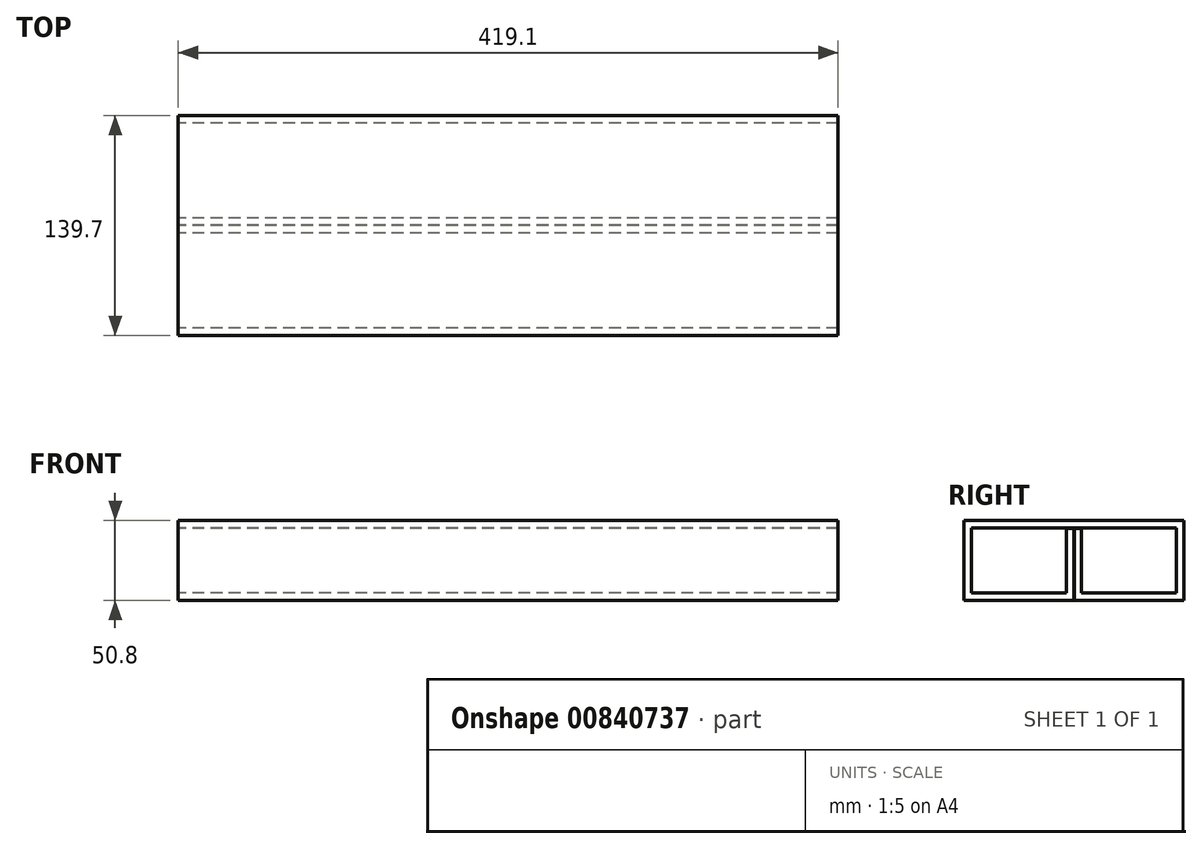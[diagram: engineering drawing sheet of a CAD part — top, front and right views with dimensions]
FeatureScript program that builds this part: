
annotation { "Feature Type Name" : "Feature", "Feature Type Description" : "" }
export const myFeature = defineFeature(function(context is Context, id is Id, definition is map)
    precondition{}
    {
        {
            var Q0;
            Q0=qCreatedBy(makeId("Right.planeOp"),FACE);
            var sketch = newSketch(context, id + "F0", { "sketchPlane" : qUnion([Q0])});
            skLineSegment(sketch, "E0", {"start": v(0, 0) * mm, "end": v(0, 126.35) * mm, "construction": true});
            skLineSegment(sketch, "E1.bottom", {"start": v(-69.85, 50.8) * mm, "end": v(69.85, 50.8) * mm});
            skLineSegment(sketch, "E1.top", {"start": v(-69.85, 0) * mm, "end": v(-0.13, 0) * mm});
            skLineSegment(sketch, "E1.left", {"start": v(-69.85, 50.8) * mm, "end": v(-69.85, 0) * mm});
            skLineSegment(sketch, "E2.0", {"start": v(-65.09, 46.04) * mm, "end": v(65.09, 46.04) * mm});
            skLineSegment(sketch, "E2.1", {"start": v(-65.09, 46.04) * mm, "end": v(-65.09, 4.76) * mm});
            skLineSegment(sketch, "E2.2", {"start": v(-65.09, 4.76) * mm, "end": v(-4.76, 4.76) * mm});
            skLineSegment(sketch, "E2.3", {"start": v(-4.76, 45.78) * mm, "end": v(-4.76, 4.76) * mm});
            skLineSegment(sketch, "E3.MirrorCS", {"start": v(69.85, 50.8) * mm, "end": v(69.85, 0) * mm});
            skLineSegment(sketch, "E4.MirrorCS", {"start": v(4.76, 45.78) * mm, "end": v(4.76, 4.76) * mm});
            skLineSegment(sketch, "E5.MirrorCS", {"start": v(65.09, 4.76) * mm, "end": v(4.76, 4.76) * mm});
            skLineSegment(sketch, "E6.MirrorCS", {"start": v(65.09, 46.04) * mm, "end": v(65.09, 4.76) * mm});
            skLineSegment(sketch, "E7.left", {"start": v(-0.13, 0) * mm, "end": v(-0.13, 45.78) * mm});
            skLineSegment(sketch, "E7.right", {"start": v(0.13, 0) * mm, "end": v(0.13, 45.78) * mm});
            skLineSegment(sketch, "E8.trimOffspring", {"start": v(0.13, 0) * mm, "end": v(69.85, 0) * mm});
            skLineSegment(sketch, "E9", {"start": v(-4.76, 45.78) * mm, "end": v(-0.13, 45.78) * mm});
            skPoint(sketch, "E10.orphan", {"position": v(4.76, 46.04) * mm});
            skLineSegment(sketch, "E11.trimOffspring", {"start": v(0.13, 45.78) * mm, "end": v(4.76, 45.78) * mm});
            skPoint(sketch, "E12.orphan", {"position": v(-4.76, 46.04) * mm});
            skSolve(sketch);
        }
        {
            var Q0;
            Q0=qSketchRegion(id+"F0",true);
            extrude(context, id + "F1", {"entities" : qUnion([Q0]), "endBound" : BoundingType.SYMMETRIC, "depth" : 419.1 * mm, "offsetDistance" : 25.4 * mm});
        }
    });
